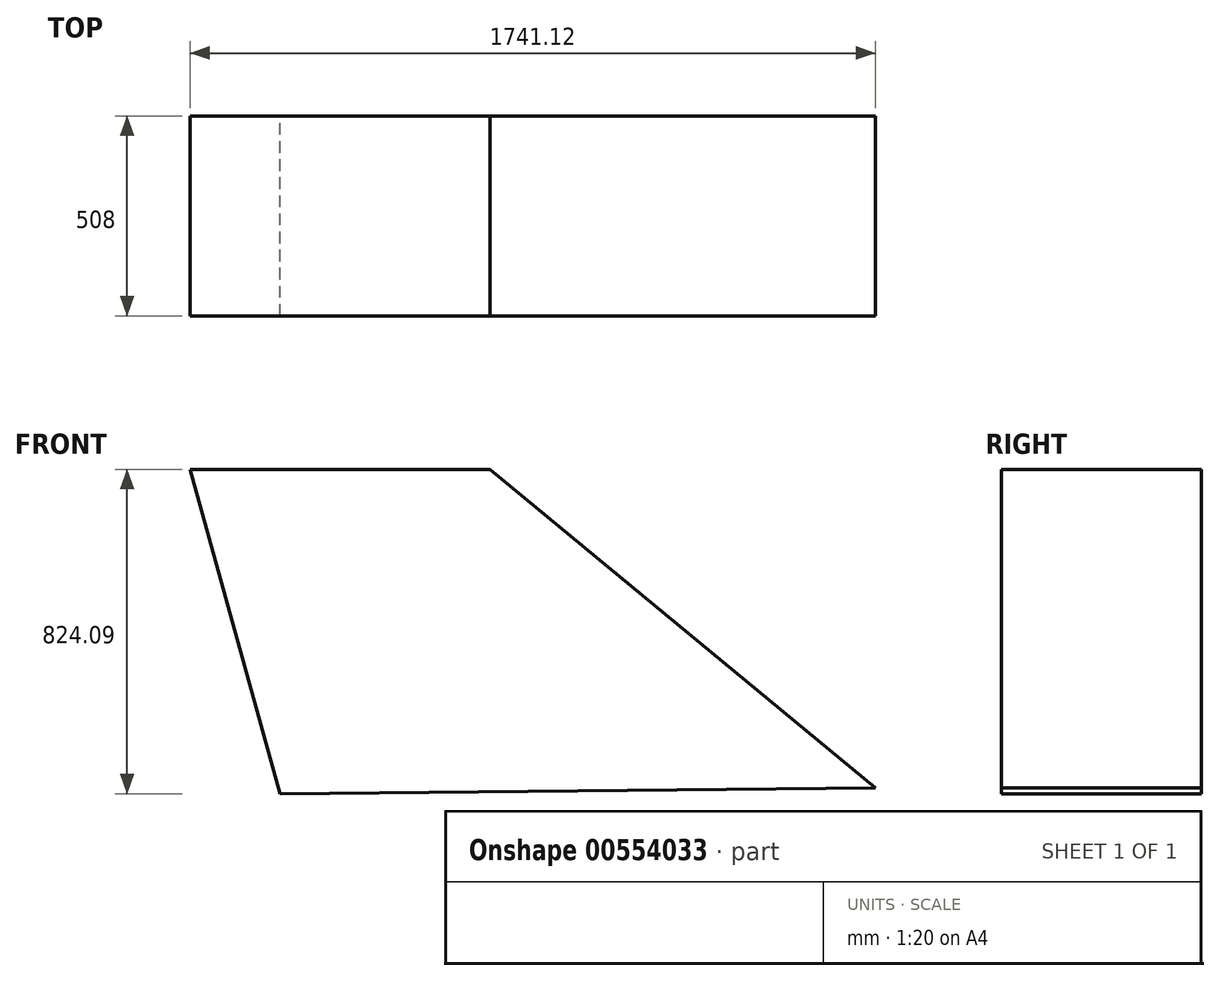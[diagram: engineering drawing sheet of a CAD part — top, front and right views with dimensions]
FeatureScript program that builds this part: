
annotation { "Feature Type Name" : "Feature", "Feature Type Description" : "" }
export const myFeature = defineFeature(function(context is Context, id is Id, definition is map)
    precondition{}
    {
        {
            var Q0;
            Q0=qCreatedBy(makeId("Front.planeOp"),FACE);
            var sketch = newSketch(context, id + "F0", { "sketchPlane" : qUnion([Q0])});
            skLineSegment(sketch, "E0", {"start": v(1349.04, -780.74) * mm, "end": v(369.92, 28.1) * mm});
            skLineSegment(sketch, "E1", {"start": v(369.92, 28.1) * mm, "end": v(-392.08, 28.1) * mm});
            skLineSegment(sketch, "E2", {"start": v(-392.08, 28.1) * mm, "end": v(-162.95, -796) * mm});
            skLineSegment(sketch, "E3", {"start": v(-162.95, -796) * mm, "end": v(1349.04, -780.74) * mm});
            skSolve(sketch);
        }
        {
            var Q0;
            Q0 = qSketchRegion(id + "F0", true);
            extrude(context, id + "F1", {"entities" : qUnion([Q0]), "depth" : 508 * mm, "offsetDistance" : 25.4 * mm});
        }
    });
